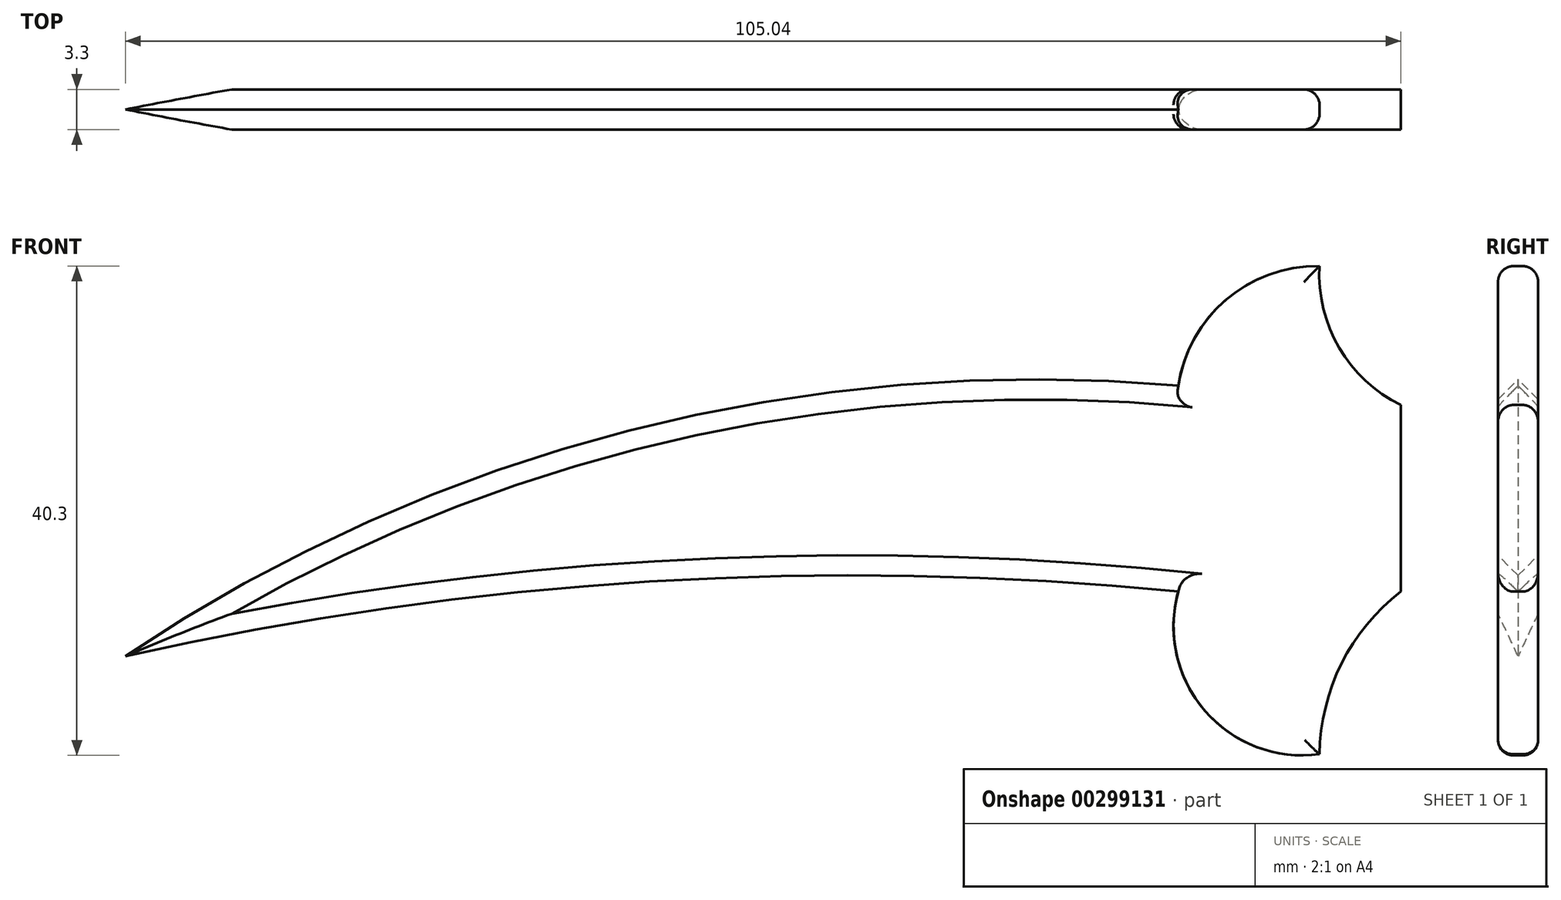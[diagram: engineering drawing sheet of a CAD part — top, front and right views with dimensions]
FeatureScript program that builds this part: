
annotation { "Feature Type Name" : "Feature", "Feature Type Description" : "" }
export const myFeature = defineFeature(function(context is Context, id is Id, definition is map)
    precondition{}
    {
        {
            var Q0;
            Q0=qCreatedBy(makeId("Front.planeOp"),FACE);
            var sketch = newSketch(context, id + "F0", { "sketchPlane" : qUnion([Q0])});
            skArc(sketch, "E0", {"start": v(9.66, 2.96) * mm, "mid": v(4.77, -2.98) * mm, "end": v(2.96, -10.44) * mm});
            skArc(sketch, "E1", {"start": v(-8.67, 2.96) * mm, "mid": v(-6.47, -6.88) * mm, "end": v(2.96, -10.44) * mm});
            skArc(sketch, "E2", {"start": v(-8.67, 2.96) * mm, "mid": v(-52.24, 3.77) * mm, "end": v(-95.38, -2.36) * mm});
            skArc(sketch, "E3", {"start": v(2.96, 29.76) * mm, "mid": v(4.58, 23.03) * mm, "end": v(9.66, 18.33) * mm});
            skArc(sketch, "E4", {"start": v(2.96, 29.76) * mm, "mid": v(-4.7, 27.02) * mm, "end": v(-8.67, 19.9) * mm});
            skArc(sketch, "E5", {"start": v(-8.67, 19.9) * mm, "mid": v(-53.94, 16.2) * mm, "end": v(-95.38, -2.36) * mm});
            skLineSegment(sketch, "E6", {"start": v(9.66, 18.33) * mm, "end": v(9.66, 2.96) * mm});
            skSolve(sketch);
        }
        {
            var Q0;
            Q0=qSketchRegion(id+"F0",true);
            extrude(context, id + "F1", {"entities" : qUnion([Q0]), "depth" : 3.3 * mm});
        }
        {
            var Q0;
            Q0=makeQuery(id+"F1.opExtrude","CAP_EDGE",EDGE,{"disambiguationData":[OSD([sQuery(id+"F0.wireOp",EDGE,"E3")])],"isStart":true});
            var Q1;
            Q1=makeQuery(id+"F1.opExtrude","CAP_EDGE",EDGE,{"disambiguationData":[OSD([sQuery(id+"F0.wireOp",EDGE,"E3")])],"isStart":false});
            var Q2;
            Q2=makeQuery(id+"F1.opExtrude","CAP_EDGE",EDGE,{"disambiguationData":[OSD([sQuery(id+"F0.wireOp",EDGE,"E0")])],"isStart":false});
            var Q3;
            Q3=makeQuery(id+"F1.opExtrude","CAP_EDGE",EDGE,{"disambiguationData":[OSD([sQuery(id+"F0.wireOp",EDGE,"E0")])],"isStart":true});
            var Q4;
            Q4=makeQuery(id+"F1.opExtrude","CAP_EDGE",EDGE,{"disambiguationData":[OSD([sQuery(id+"F0.wireOp",EDGE,"8e2cOCSa-u8oL-kPB0-iw2g-2OpoCuylEIHE")])],"isStart":false});
            var Q5;
            Q5=makeQuery(id+"F1.opExtrude","CAP_EDGE",EDGE,{"disambiguationData":[OSD([sQuery(id+"F0.wireOp",EDGE,"t7sjEmGu-ZfWW-NZeB-DM5r-nfLMW1VtfxVX")])],"isStart":false});
            var Q6;
            Q6=makeQuery(id+"F1.opExtrude","CAP_EDGE",EDGE,{"disambiguationData":[OSD([sQuery(id+"F0.wireOp",EDGE,"t7sjEmGu-ZfWW-NZeB-DM5r-nfLMW1VtfxVX")])],"isStart":true});
            var Q7;
            Q7=makeQuery(id+"F1.opExtrude","CAP_EDGE",EDGE,{"disambiguationData":[OSD([sQuery(id+"F0.wireOp",EDGE,"8e2cOCSa-u8oL-kPB0-iw2g-2OpoCuylEIHE")])],"isStart":true});
            var Q8;
            Q8=makeQuery(id+"F1.opExtrude","CAP_EDGE",EDGE,{"disambiguationData":[OSD([sQuery(id+"F0.wireOp",EDGE,"pNwqxSXR-W5zd-gGHY-HGur-oaw1MPE9jJMv")])],"isStart":true});
            var Q9;
            Q9=makeQuery(id+"F1.opExtrude","CAP_EDGE",EDGE,{"disambiguationData":[OSD([sQuery(id+"F0.wireOp",EDGE,"8guZ14HR-FmJ8-1mOu-uOkM-tSYQRnn4MZCO")])],"isStart":true});
            var Q10;
            Q10=makeQuery(id+"F1.opExtrude","CAP_EDGE",EDGE,{"disambiguationData":[OSD([sQuery(id+"F0.wireOp",EDGE,"TT4Pfhk2-l6Jf-pxnm-g7Q8-Ewikwd5y7BnD")])],"isStart":true});
            var Q11;
            Q11=makeQuery(id+"F1.opExtrude","CAP_EDGE",EDGE,{"disambiguationData":[OSD([sQuery(id+"F0.wireOp",EDGE,"m4Tqzzhf-yzKG-XgRF-O08W-39QF0HdPqliM")])],"isStart":true});
            var Q12;
            Q12=makeQuery(id+"F1.opExtrude","CAP_EDGE",EDGE,{"disambiguationData":[OSD([sQuery(id+"F0.wireOp",EDGE,"jkLd4orJ-ONJx-gaGE-4OfS-Hdzt1qF71cSd")])],"isStart":true});
            var Q13;
            Q13=makeQuery(id+"F1.opExtrude","CAP_EDGE",EDGE,{"disambiguationData":[OSD([sQuery(id+"F0.wireOp",EDGE,"jkLd4orJ-ONJx-gaGE-4OfS-Hdzt1qF71cSd")])],"isStart":false});
            var Q14;
            Q14=makeQuery(id+"F1.opExtrude","CAP_EDGE",EDGE,{"disambiguationData":[OSD([sQuery(id+"F0.wireOp",EDGE,"m4Tqzzhf-yzKG-XgRF-O08W-39QF0HdPqliM")])],"isStart":false});
            var Q15;
            Q15=makeQuery(id+"F1.opExtrude","CAP_EDGE",EDGE,{"disambiguationData":[OSD([sQuery(id+"F0.wireOp",EDGE,"pNwqxSXR-W5zd-gGHY-HGur-oaw1MPE9jJMv")])],"isStart":false});
            var Q16;
            Q16=makeQuery(id+"F1.opExtrude","CAP_EDGE",EDGE,{"disambiguationData":[OSD([sQuery(id+"F0.wireOp",EDGE,"8guZ14HR-FmJ8-1mOu-uOkM-tSYQRnn4MZCO")])],"isStart":false});
            var Q17;
            Q17=makeQuery(id+"F1.opExtrude","CAP_EDGE",EDGE,{"disambiguationData":[OSD([sQuery(id+"F0.wireOp",EDGE,"TT4Pfhk2-l6Jf-pxnm-g7Q8-Ewikwd5y7BnD")])],"isStart":false});
            var Q18;
            Q18=makeQuery(id+"F1.opExtrude","CAP_EDGE",EDGE,{"disambiguationData":[OSD([sQuery(id+"F0.wireOp",EDGE,"E4")])],"isStart":false});
            var Q19;
            Q19=makeQuery(id+"F1.opExtrude","CAP_EDGE",EDGE,{"disambiguationData":[OSD([sQuery(id+"F0.wireOp",EDGE,"E4")])],"isStart":true});
            var Q20;
            Q20=makeQuery(id+"F1.opExtrude","CAP_EDGE",EDGE,{"disambiguationData":[OSD([sQuery(id+"F0.wireOp",EDGE,"E1")])],"isStart":false});
            var Q21;
            Q21=makeQuery(id+"F1.opExtrude","CAP_EDGE",EDGE,{"disambiguationData":[OSD([sQuery(id+"F0.wireOp",EDGE,"E1")])],"isStart":true});
            fillet(context, id + "F2", {"entities" : qUnion([Q0, Q1, Q2, Q3, Q4, Q5, Q6, Q7, Q8, Q9, Q10, Q11, Q12, Q13, Q14, Q15, Q16, Q17, Q18, Q19, Q20, Q21]), "radius" : 1.27 * mm, "tangentPropagation" : true, "allowEdgeOverflow" : false});
        }
        {
            var Q0;
            Q0=makeQuery(id+"F1.opExtrude","CAP_EDGE",EDGE,{"disambiguationData":[OSD([sQuery(id+"F0.wireOp",EDGE,"E5")])],"isStart":true});
            var Q1;
            Q1=makeQuery(id+"F1.opExtrude","CAP_EDGE",EDGE,{"disambiguationData":[OSD([sQuery(id+"F0.wireOp",EDGE,"E2")])],"isStart":true});
            var Q2;
            Q2=makeQuery(id+"F1.opExtrude","CAP_EDGE",EDGE,{"disambiguationData":[OSD([sQuery(id+"F0.wireOp",EDGE,"E5")])],"isStart":false});
            var Q3;
            Q3=makeQuery(id+"F1.opExtrude","CAP_EDGE",EDGE,{"disambiguationData":[OSD([sQuery(id+"F0.wireOp",EDGE,"E2")])],"isStart":false});
            chamfer(context, id + "F3", {"entities" : qUnion([Q0, Q1, Q2, Q3]), "width" : 1.65 * mm, "tangentPropagation" : true});
        }
    });
